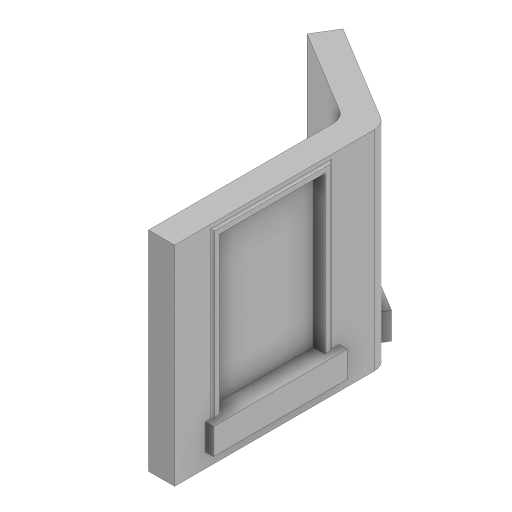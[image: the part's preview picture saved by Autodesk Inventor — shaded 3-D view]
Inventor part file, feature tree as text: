
AUTODESK INVENTOR PART (.ipt)
format: ipt  version: 2023 (Build 270158000, 158)  size: 287,232 bytes
history: native  units: in
note: dims shown in document units (in); Inventor stores cm internally (conversion verified against a paired STEP export)
features: extrude x8, sketch x8, projected_geometry x8, fillet x4, plane x1
ambient origin geometry x8: Origin, YZ Plane, XZ Plane, XY Plane, X Axis, Y Axis, Z Axis, Center Point
bodies: Solid1 (feature_tree)
feature tree (29):
  extrude  "Extrusion1"  Depth=157.4803in
  extrude  "Extrusion4"  Depth=19.685in
  fillet  "Fillet2"  Radius=2.0in
  fillet  "Fillet3"  Radius=12.0in
  fillet  "Fillet4"  Radius=9.8425in
  extrude  "Extrusion5"  Depth=39.3701in TaperAngle=0.0deg
  plane  "Work Plane3"
  extrude  "Extrusion6"  [1 undecoded]
  extrude  "Extrusion7"  Depth=1.0in TaperAngle=0.0deg
  extrude  "Extrusion8"  Depth=1.0in TaperAngle=0.0deg
  fillet  "Fillet5"  Radius=2.0in
  extrude  "Extrusion9"  Depth=6.0in TaperAngle=0.0deg
  extrude  "Extrusion10"  [1 undecoded]
  sketch  "Sketch1"  dims[d0=19.685in d1=157.4803in]
  sketch  "Sketch2"  dims[d2=118.1102in d3=0.0in d18=19.685in d19=2.0in d20=0.0in d21=12.0in d22=9.8425in]
  projected_geometry  "Projected Loop1"
  sketch  "Sketch4"  dims[d23=9.8425in d24=39.3701in d25=0.0in]
  projected_geometry  "Projected Loop3"
  sketch  "Sketch5"  dims[d26=118.1102in d27=0.0in d28=-30.5625in]
  projected_geometry  "Projected Loop4"
  sketch  "Sketch6"  dims[d29=4.0in d30=1.0in d31=0.0in]
  projected_geometry  "Projected Loop5"
  sketch  "Sketch7"  dims[d32=4.0in d33=1.0in d34=0.0in d35=2.0in]
  projected_geometry  "Projected Loop6"
  sketch  "Sketch8"  dims[d36=6.0in d37=0.0in d38=6.0in d39=0.0in]
  projected_geometry  "Projected Loop7"
  sketch  "Sketch9"
  projected_geometry  "Projected Loop8"
  projected_geometry  "Projected Loop9"
note: 2 required parameter values undecoded (feature->parameter linkage not recoverable at this tier; creation-order binding heuristic only, values carry confidence <= 0.55)
